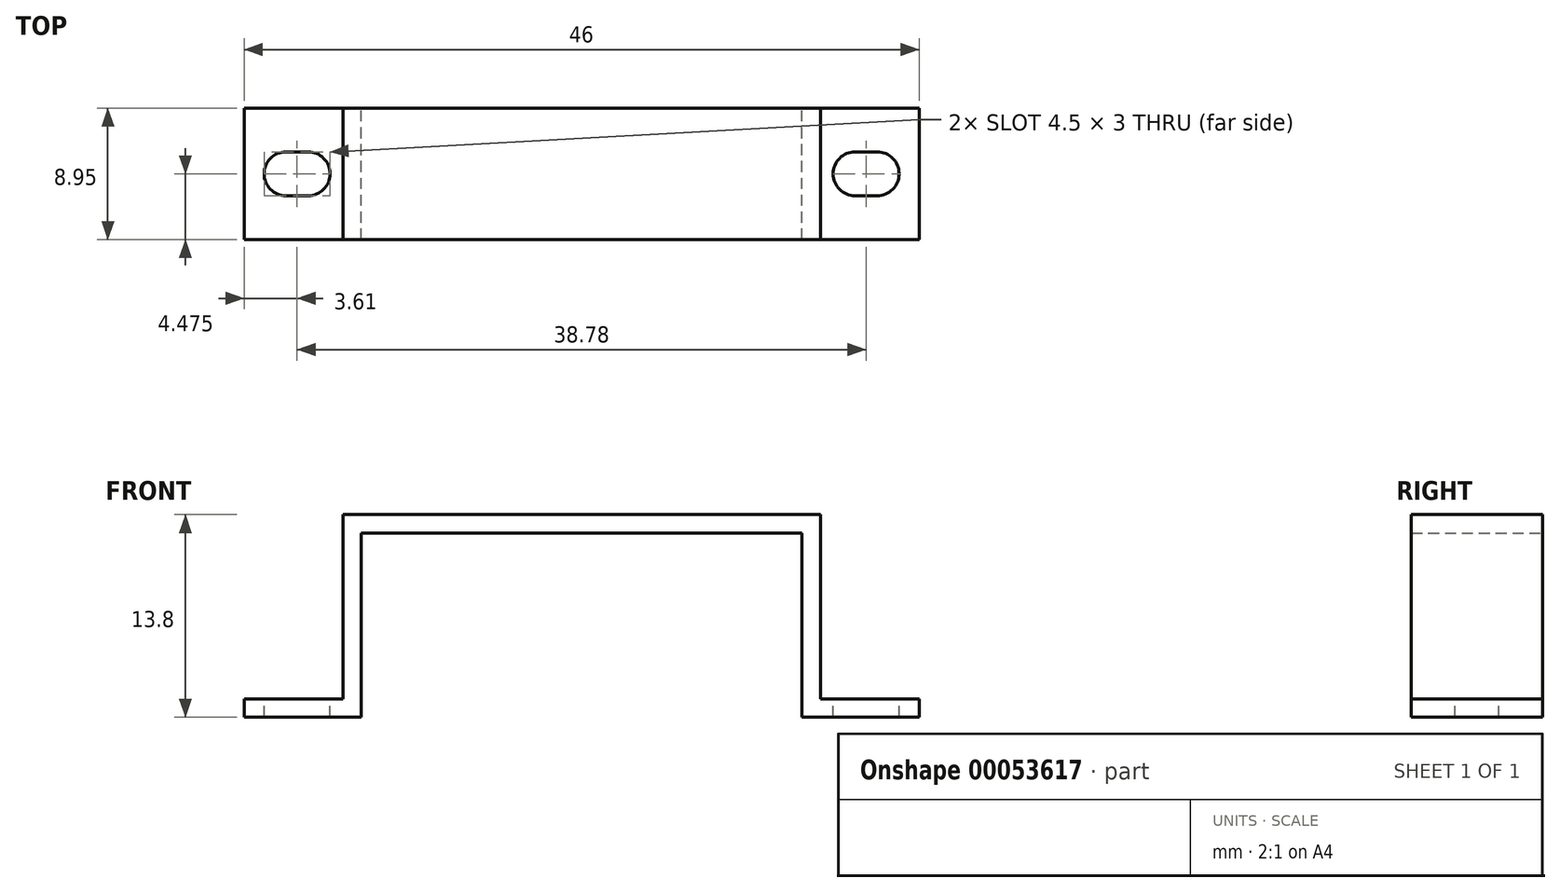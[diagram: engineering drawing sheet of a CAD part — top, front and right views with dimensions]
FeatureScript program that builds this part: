
annotation { "Feature Type Name" : "Feature", "Feature Type Description" : "" }
export const myFeature = defineFeature(function(context is Context, id is Id, definition is map)
    precondition{}
    {
        {
            var Q0;
            Q0=qCreatedBy(makeId("Front.planeOp"),FACE);
            var sketch = newSketch(context, id + "F0", { "sketchPlane" : qUnion([Q0])});
            skLineSegment(sketch, "E0.bottom", {"start": v(-23, 0) * mm, "end": v(23, 0) * mm});
            skLineSegment(sketch, "E0.top", {"start": v(-23, 13.8) * mm, "end": v(23, 13.8) * mm});
            skLineSegment(sketch, "E0.left", {"start": v(-23, 0) * mm, "end": v(-23, 13.8) * mm});
            skLineSegment(sketch, "E0.right", {"start": v(23, 0) * mm, "end": v(23, 13.8) * mm});
            skLineSegment(sketch, "E1.bottom", {"start": v(-15.03, 0) * mm, "end": v(15.03, 0) * mm});
            skLineSegment(sketch, "E1.top", {"start": v(-15.03, 12.55) * mm, "end": v(15.02, 12.55) * mm});
            skLineSegment(sketch, "E1.left", {"start": v(-15.02, 0) * mm, "end": v(-15.03, 12.55) * mm});
            skLineSegment(sketch, "E1.right", {"start": v(15.03, 0) * mm, "end": v(15.02, 12.55) * mm});
            skLineSegment(sketch, "E2", {"start": v(-23, 1.25) * mm, "end": v(23, 1.25) * mm});
            skLineSegment(sketch, "E3", {"start": v(-16.27, 13.8) * mm, "end": v(-16.27, 0) * mm});
            skLineSegment(sketch, "E4", {"start": v(16.28, 13.8) * mm, "end": v(16.28, 0) * mm});
            skSolve(sketch);
        }
        {
            var Q0;
            {var subQ0=sQuery(id+"F0.wireOp",EDGE,"E0.left");var subQ1=sQuery(id+"F0.wireOp",EDGE,"E0.bottom");var subQ2=makeQuery(id+"F0.imprint","INTERSECT",VERTEX,{"derivedFrom":[subQ1,subQ0]});Q0=makeQuery(id+"F0.imprint","IMPRINT",FACE,{"disambiguationData":[TD([[makeQuery(id+"F0.imprint","IMPRINT",EDGE,{"disambiguationData":[TD([[subQ2,-1.0]])],"derivedFrom":subQ1}),1.0]])]});}
            var Q1;
            {var subQ0=sQuery(id+"F0.wireOp",EDGE,"E1.left");var subQ5=sQuery(id+"F0.wireOp",EDGE,"E2");var subQ6=makeQuery(id+"F0.imprint","INTERSECT",VERTEX,{"derivedFrom":[subQ0,subQ5]});Q1=makeQuery(id+"F0.imprint","IMPRINT",FACE,{"disambiguationData":[TD([[makeQuery(id+"F0.imprint","IMPRINT",EDGE,{"disambiguationData":[TD([[subQ6,1.0]])],"derivedFrom":subQ5}),-1.0]])]});}
            var Q2;
            {var subQ1=sQuery(id+"F0.wireOp",EDGE,"E1.top");Q2=makeQuery(id+"F0.imprint","IMPRINT",FACE,{"disambiguationData":[TD([[makeQuery(id+"F0.imprint","IMPRINT",EDGE,{"derivedFrom":subQ1}),1.0]])]});}
            var Q3;
            {var subQ0=sQuery(id+"F0.wireOp",EDGE,"E1.right");var subQ5=sQuery(id+"F0.wireOp",EDGE,"E2");var subQ6=makeQuery(id+"F0.imprint","INTERSECT",VERTEX,{"derivedFrom":[subQ0,subQ5]});Q3=makeQuery(id+"F0.imprint","IMPRINT",FACE,{"disambiguationData":[TD([[makeQuery(id+"F0.imprint","IMPRINT",EDGE,{"disambiguationData":[TD([[subQ6,-1.0]])],"derivedFrom":subQ5}),-1.0]])]});}
            var Q4;
            {var subQ0=sQuery(id+"F0.wireOp",EDGE,"E0.right");var subQ1=sQuery(id+"F0.wireOp",EDGE,"E0.bottom");var subQ2=makeQuery(id+"F0.imprint","INTERSECT",VERTEX,{"derivedFrom":[subQ1,subQ0]});Q4=makeQuery(id+"F0.imprint","IMPRINT",FACE,{"disambiguationData":[TD([[makeQuery(id+"F0.imprint","IMPRINT",EDGE,{"disambiguationData":[TD([[subQ2,1.0]])],"derivedFrom":subQ1}),1.0]])]});}
            extrude(context, id + "F1", {"entities" : qUnion([Q0, Q1, Q2, Q3, Q4]), "depth" : 8.95 * mm});
        }
        {
            var Q0;
            {var subQ0=sQuery(id+"F0.wireOp",EDGE,"E2");Q0=makeQuery(id+"F1.opExtrude","SWEPT_FACE",FACE,{"disambiguationData":[OSD([subQ0]),TDD([makeQuery(id+"F0.imprint","IMPRINT",EDGE,{"disambiguationData":[TD([[makeQuery(id+"F0.imprint","INTERSECT",VERTEX,{"derivedFrom":[sQuery(id+"F0.wireOp",EDGE,"E0.left"),subQ0]}),-1.0]])],"derivedFrom":subQ0})])]});}
            var sketch = newSketch(context, id + "F2", { "sketchPlane" : qUnion([Q0])});
            skCircle(sketch, "E5", {"center": v(-18.64, -4.48) * mm, "radius": 1.5 * mm});
            skCircle(sketch, "E6", {"center": v(18.64, -4.48) * mm, "radius": 1.5 * mm});
            skLineSegment(sketch, "E7.0", {"start": v(23, -8.95) * mm, "end": v(23, 0) * mm});
            skLineSegment(sketch, "E7.1", {"start": v(-23, -8.95) * mm, "end": v(-23, 0) * mm});
            skLineSegment(sketch, "E8", {"start": v(23, -4.48) * mm, "end": v(-23, -4.48) * mm, "construction": true});
            skLineSegment(sketch, "E9", {"start": v(18.64, -4.48) * mm, "end": v(-18.64, -4.48) * mm});
            skCircle(sketch, "E10", {"center": v(-20.14, -4.48) * mm, "radius": 1.5 * mm});
            skLineSegment(sketch, "E11", {"start": v(-20.14, -2.98) * mm, "end": v(-18.64, -2.98) * mm});
            skLineSegment(sketch, "E12", {"start": v(-20.14, -5.98) * mm, "end": v(-18.64, -5.98) * mm});
            skLineSegment(sketch, "E13", {"start": v(0, 0) * mm, "end": v(0, -10.02) * mm, "construction": true});
            skLineSegment(sketch, "E14.MirrorCS", {"start": v(20.14, -2.98) * mm, "end": v(18.64, -2.98) * mm});
            skCircle(sketch, "E15.MirrorC", {"center": v(20.14, -4.48) * mm, "radius": 1.5 * mm});
            skLineSegment(sketch, "E16.MirrorCS", {"start": v(20.14, -5.98) * mm, "end": v(18.64, -5.98) * mm});
            skSolve(sketch);
        }
        {
            var Q0;
            {var subQ0=sQuery(id+"F2.wireOp",EDGE,"E11");Q0=makeQuery(id+"F2.imprint","IMPRINT",FACE,{"disambiguationData":[TD([[makeQuery(id+"F2.imprint","IMPRINT",EDGE,{"derivedFrom":subQ0}),-1.0]])]});}
            var Q1;
            {var subQ0=sQuery(id+"F2.wireOp",EDGE,"E10");var subQ1=sQuery(id+"F2.wireOp",EDGE,"E5");var subQ2=makeQuery(id+"F2.imprint","INTERSECT",VERTEX,{"disambiguationData":[OD(0.0)],"derivedFrom":[subQ1,subQ0]});Q1=makeQuery(id+"F2.imprint","IMPRINT",FACE,{"disambiguationData":[TD([[makeQuery(id+"F2.imprint","IMPRINT",EDGE,{"disambiguationData":[TD([[subQ2,-1.0]])],"derivedFrom":subQ1}),-1.0]])]});}
            var Q2;
            {var subQ0=sQuery(id+"F2.wireOp",EDGE,"E10");var subQ1=sQuery(id+"F2.wireOp",EDGE,"E5");var subQ2=makeQuery(id+"F2.imprint","INTERSECT",VERTEX,{"disambiguationData":[OD(0.0)],"derivedFrom":[subQ1,subQ0]});Q2=makeQuery(id+"F2.imprint","IMPRINT",FACE,{"disambiguationData":[TD([[makeQuery(id+"F2.imprint","IMPRINT",EDGE,{"disambiguationData":[TD([[subQ2,-1.0]])],"derivedFrom":subQ1}),1.0]])]});}
            var Q3;
            {var subQ0=sQuery(id+"F2.wireOp",EDGE,"E5");var subQ1=makeQuery(id+"F2.imprint","INTERSECT",VERTEX,{"derivedFrom":[subQ0,sQuery(id+"F2.wireOp",EDGE,"E11")]});Q3=makeQuery(id+"F2.imprint","IMPRINT",FACE,{"disambiguationData":[TD([[makeQuery(id+"F2.imprint","IMPRINT",EDGE,{"disambiguationData":[TD([[subQ1,1.0]])],"derivedFrom":subQ0}),1.0]])]});}
            var Q4;
            {var subQ0=sQuery(id+"F2.wireOp",EDGE,"E5");var subQ1=makeQuery(id+"F2.imprint","INTERSECT",VERTEX,{"derivedFrom":[subQ0,sQuery(id+"F2.wireOp",EDGE,"E12")]});Q4=makeQuery(id+"F2.imprint","IMPRINT",FACE,{"disambiguationData":[TD([[makeQuery(id+"F2.imprint","IMPRINT",EDGE,{"disambiguationData":[TD([[subQ1,1.0]])],"derivedFrom":subQ0}),1.0]])]});}
            var Q5;
            {var subQ0=sQuery(id+"F2.wireOp",EDGE,"E12");Q5=makeQuery(id+"F2.imprint","IMPRINT",FACE,{"disambiguationData":[TD([[makeQuery(id+"F2.imprint","IMPRINT",EDGE,{"derivedFrom":subQ0}),1.0]])]});}
            var Q6;
            {var subQ0=sQuery(id+"F2.wireOp",EDGE,"E14.MirrorCS");Q6=makeQuery(id+"F2.imprint","IMPRINT",FACE,{"disambiguationData":[TD([[makeQuery(id+"F2.imprint","IMPRINT",EDGE,{"derivedFrom":subQ0}),1.0]])]});}
            var Q7;
            {var subQ0=sQuery(id+"F2.wireOp",EDGE,"E6");var subQ1=makeQuery(id+"F2.imprint","INTERSECT",VERTEX,{"derivedFrom":[subQ0,sQuery(id+"F2.wireOp",EDGE,"E14.MirrorCS")]});Q7=makeQuery(id+"F2.imprint","IMPRINT",FACE,{"disambiguationData":[TD([[makeQuery(id+"F2.imprint","IMPRINT",EDGE,{"disambiguationData":[TD([[subQ1,1.0]])],"derivedFrom":subQ0}),1.0]])]});}
            var Q8;
            {var subQ0=sQuery(id+"F2.wireOp",EDGE,"E15.MirrorC");var subQ1=sQuery(id+"F2.wireOp",EDGE,"E6");var subQ2=makeQuery(id+"F2.imprint","INTERSECT",VERTEX,{"disambiguationData":[OD(0.0)],"derivedFrom":[subQ1,subQ0]});Q8=makeQuery(id+"F2.imprint","IMPRINT",FACE,{"disambiguationData":[TD([[makeQuery(id+"F2.imprint","IMPRINT",EDGE,{"disambiguationData":[TD([[subQ2,1.0]])],"derivedFrom":subQ1}),1.0]])]});}
            var Q9;
            {var subQ0=sQuery(id+"F2.wireOp",EDGE,"E15.MirrorC");var subQ1=sQuery(id+"F2.wireOp",EDGE,"E6");var subQ2=makeQuery(id+"F2.imprint","INTERSECT",VERTEX,{"disambiguationData":[OD(0.0)],"derivedFrom":[subQ1,subQ0]});Q9=makeQuery(id+"F2.imprint","IMPRINT",FACE,{"disambiguationData":[TD([[makeQuery(id+"F2.imprint","IMPRINT",EDGE,{"disambiguationData":[TD([[subQ2,1.0]])],"derivedFrom":subQ1}),-1.0]])]});}
            var Q10;
            {var subQ0=sQuery(id+"F2.wireOp",EDGE,"E16.MirrorCS");Q10=makeQuery(id+"F2.imprint","IMPRINT",FACE,{"disambiguationData":[TD([[makeQuery(id+"F2.imprint","IMPRINT",EDGE,{"derivedFrom":subQ0}),-1.0]])]});}
            var Q11;
            {var subQ0=sQuery(id+"F2.wireOp",EDGE,"E6");var subQ1=makeQuery(id+"F2.imprint","INTERSECT",VERTEX,{"derivedFrom":[subQ0,sQuery(id+"F2.wireOp",EDGE,"E16.MirrorCS")]});Q11=makeQuery(id+"F2.imprint","IMPRINT",FACE,{"disambiguationData":[TD([[makeQuery(id+"F2.imprint","IMPRINT",EDGE,{"disambiguationData":[TD([[subQ1,1.0]])],"derivedFrom":subQ0}),1.0]])]});}
            extrude(context, id + "F3", {"entities" : qUnion([Q0, Q1, Q2, Q3, Q4, Q5, Q6, Q7, Q8, Q9, Q10, Q11]), "operationType" : NewBodyOperationType.REMOVE, "oppositeDirection" : true, "depth" : 25 * mm});
        }
    });
